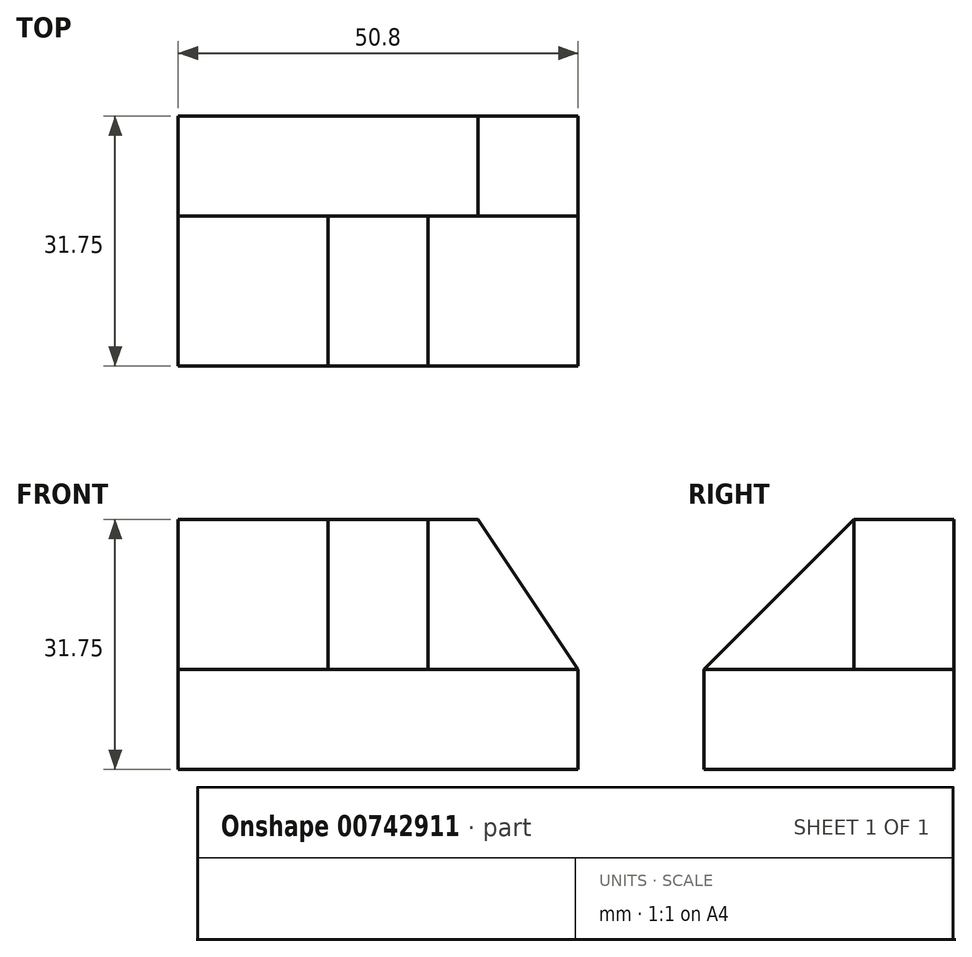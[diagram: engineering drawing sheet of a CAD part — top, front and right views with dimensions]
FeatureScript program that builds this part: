
annotation { "Feature Type Name" : "Feature", "Feature Type Description" : "" }
export const myFeature = defineFeature(function(context is Context, id is Id, definition is map)
    precondition{}
    {
        {
            var Q0;
            Q0=qCreatedBy(makeId("Front.planeOp"),FACE);
            var sketch = newSketch(context, id + "F0", { "sketchPlane" : qUnion([Q0])});
            skLineSegment(sketch, "E0", {"start": v(0, 0) * mm, "end": v(50.8, 0) * mm});
            skLineSegment(sketch, "E1", {"start": v(50.8, 0) * mm, "end": v(50.8, 12.7) * mm});
            skLineSegment(sketch, "E2", {"start": v(50.8, 12.7) * mm, "end": v(38.1, 31.75) * mm});
            skLineSegment(sketch, "E3", {"start": v(38.1, 31.75) * mm, "end": v(0, 31.75) * mm});
            skLineSegment(sketch, "E4", {"start": v(0, 31.75) * mm, "end": v(0, 31.75) * mm});
            skLineSegment(sketch, "E5", {"start": v(0, 31.75) * mm, "end": v(0, 0) * mm});
            skSolve(sketch);
        }
        {
            var Q0;
            Q0=makeQuery(id+"F0.imprint","IMPRINT",FACE,{"disambiguationData":[TD([[makeQuery(id+"F0.imprint","IMPRINT",EDGE,{"derivedFrom":sQuery(id+"F0.wireOp",EDGE,"E0")}),1.0]])]});
            extrude(context, id + "F1", {"entities" : qUnion([Q0]), "oppositeDirection" : true, "depth" : 31.75 * mm, "offsetDistance" : 25.4 * mm});
        }
        {
            var Q0;
            Q0=makeQuery(id+"F1.opExtrude","CAP_FACE",FACE,{"disambiguationData":[OSD([sQuery(id+"F0.wireOp",EDGE,"E0"),sQuery(id+"F0.wireOp",EDGE,"E1"),sQuery(id+"F0.wireOp",EDGE,"E2"),sQuery(id+"F0.wireOp",EDGE,"E3"),sQuery(id+"F0.wireOp",EDGE,"E5")])],"isStart":true});
            var sketch = newSketch(context, id + "F2", { "sketchPlane" : qUnion([Q0])});
            skLineSegment(sketch, "E6", {"start": v(50.8, 12.7) * mm, "end": v(31.75, 12.7) * mm});
            skLineSegment(sketch, "E7", {"start": v(31.75, 12.7) * mm, "end": v(31.75, 31.75) * mm});
            skLineSegment(sketch, "E8", {"start": v(31.75, 31.75) * mm, "end": v(38.1, 31.75) * mm});
            skLineSegment(sketch, "E9", {"start": v(38.1, 31.75) * mm, "end": v(50.8, 12.7) * mm});
            skSolve(sketch);
        }
        {
            var Q0;
            Q0=makeQuery(id+"F2.imprint","IMPRINT",FACE,{"disambiguationData":[TD([[makeQuery(id+"F2.imprint","IMPRINT",EDGE,{"derivedFrom":sQuery(id+"F2.wireOp",EDGE,"E6")}),-1.0]])]});
            extrude(context, id + "F3", {"entities" : qUnion([Q0]), "operationType" : NewBodyOperationType.REMOVE, "oppositeDirection" : true, "depth" : 19.05 * mm, "offsetDistance" : 25.4 * mm});
        }
        {
            var Q0;
            Q0=makeQuery(id+"F1.opExtrude","CAP_FACE",FACE,{"disambiguationData":[OSD([sQuery(id+"F0.wireOp",EDGE,"E0"),sQuery(id+"F0.wireOp",EDGE,"E1"),sQuery(id+"F0.wireOp",EDGE,"E2"),sQuery(id+"F0.wireOp",EDGE,"E3"),sQuery(id+"F0.wireOp",EDGE,"E5")])],"isStart":true});
            var sketch = newSketch(context, id + "F4", { "sketchPlane" : qUnion([Q0])});
            skLineSegment(sketch, "E10", {"start": v(19.05, 31.75) * mm, "end": v(19.05, 12.7) * mm});
            skLineSegment(sketch, "E11", {"start": v(19.05, 12.7) * mm, "end": v(0, 12.7) * mm});
            skLineSegment(sketch, "E12", {"start": v(0, 12.7) * mm, "end": v(0, 31.75) * mm});
            skLineSegment(sketch, "E13", {"start": v(0, 31.75) * mm, "end": v(19.05, 31.75) * mm});
            skSolve(sketch);
        }
        {
            var Q0;
            Q0=makeQuery(id+"F4.imprint","IMPRINT",FACE,{"disambiguationData":[TD([[makeQuery(id+"F4.imprint","IMPRINT",EDGE,{"derivedFrom":sQuery(id+"F4.wireOp",EDGE,"E10")}),-1.0]])]});
            extrude(context, id + "F5", {"entities" : qUnion([Q0]), "operationType" : NewBodyOperationType.REMOVE, "oppositeDirection" : true, "depth" : 19.05 * mm, "offsetDistance" : 25.4 * mm});
        }
        {
            var Q0;
            Q0=makeQuery(id+"F3.boolean.opBoolean","COPY",FACE,{"derivedFrom":makeQuery(id+"F3.opExtrude","SWEPT_FACE",FACE,{"disambiguationData":[OSD([sQuery(id+"F2.wireOp",EDGE,"E7")])]})});
            var sketch = newSketch(context, id + "F6", { "sketchPlane" : qUnion([Q0])});
            skLineSegment(sketch, "E14", {"start": v(19.05, 31.75) * mm, "end": v(0, 12.7) * mm});
            skLineSegment(sketch, "E15", {"start": v(0, 12.7) * mm, "end": v(0, 31.75) * mm});
            skLineSegment(sketch, "E16", {"start": v(0, 31.75) * mm, "end": v(19.05, 31.75) * mm});
            skSolve(sketch);
        }
        {
            var Q0;
            Q0=makeQuery(id+"F6.imprint","IMPRINT",FACE,{"disambiguationData":[TD([[makeQuery(id+"F6.imprint","IMPRINT",EDGE,{"derivedFrom":sQuery(id+"F6.wireOp",EDGE,"E14")}),-1.0]])]});
            extrude(context, id + "F7", {"entities" : qUnion([Q0]), "operationType" : NewBodyOperationType.REMOVE, "oppositeDirection" : true, "depth" : 25.4 * mm, "offsetDistance" : 25.4 * mm});
        }
    });
